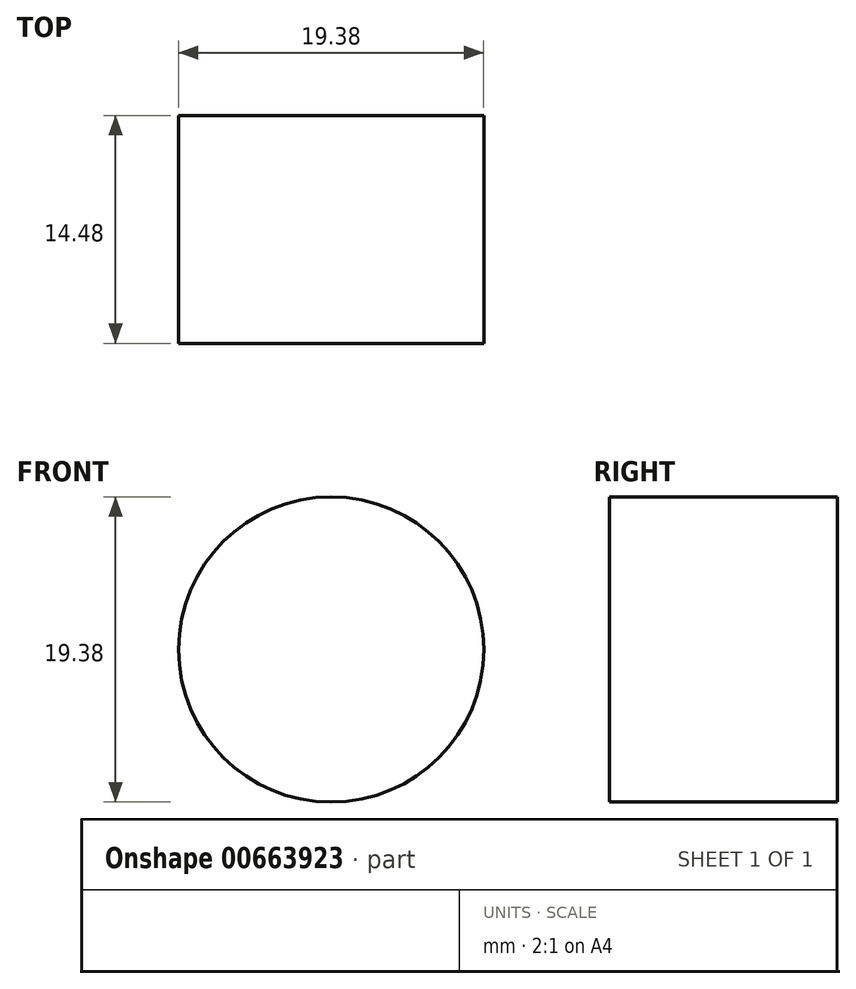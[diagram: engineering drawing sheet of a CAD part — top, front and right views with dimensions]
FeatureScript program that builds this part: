
annotation { "Feature Type Name" : "Feature", "Feature Type Description" : "" }
export const myFeature = defineFeature(function(context is Context, id is Id, definition is map)
    precondition{}
    {
        {
            var Q0;
            Q0=qCreatedBy(makeId("Front.planeOp"),FACE);
            var sketch = newSketch(context, id + "F0", { "sketchPlane" : qUnion([Q0])});
            skCircle(sketch, "E0", {"center": v(-125.99, 22.57) * mm, "radius": 9.7 * mm});
            skSolve(sketch);
        }
        {
            var Q0;
            Q0 = qSketchRegion(id + "F0", true);
            extrude(context, id + "F1", {"entities" : qUnion([Q0]), "depth" : -8.9 * mm, "offsetDistance" : 25.4 * mm});
        }
        {
            var Q0;
            Q0=makeQuery(id+"F1.opExtrude","CAP_FACE",FACE,{"disambiguationData":[OSD([sQuery(id+"F0.wireOp",EDGE,"E0")])],"isStart":true});
            extrude(context, id + "F2", {"entities" : qUnion([Q0]), "operationType" : NewBodyOperationType.ADD, "oppositeDirection" : true, "depth" : 14.48 * mm, "offsetDistance" : 25.4 * mm});
        }
    });
